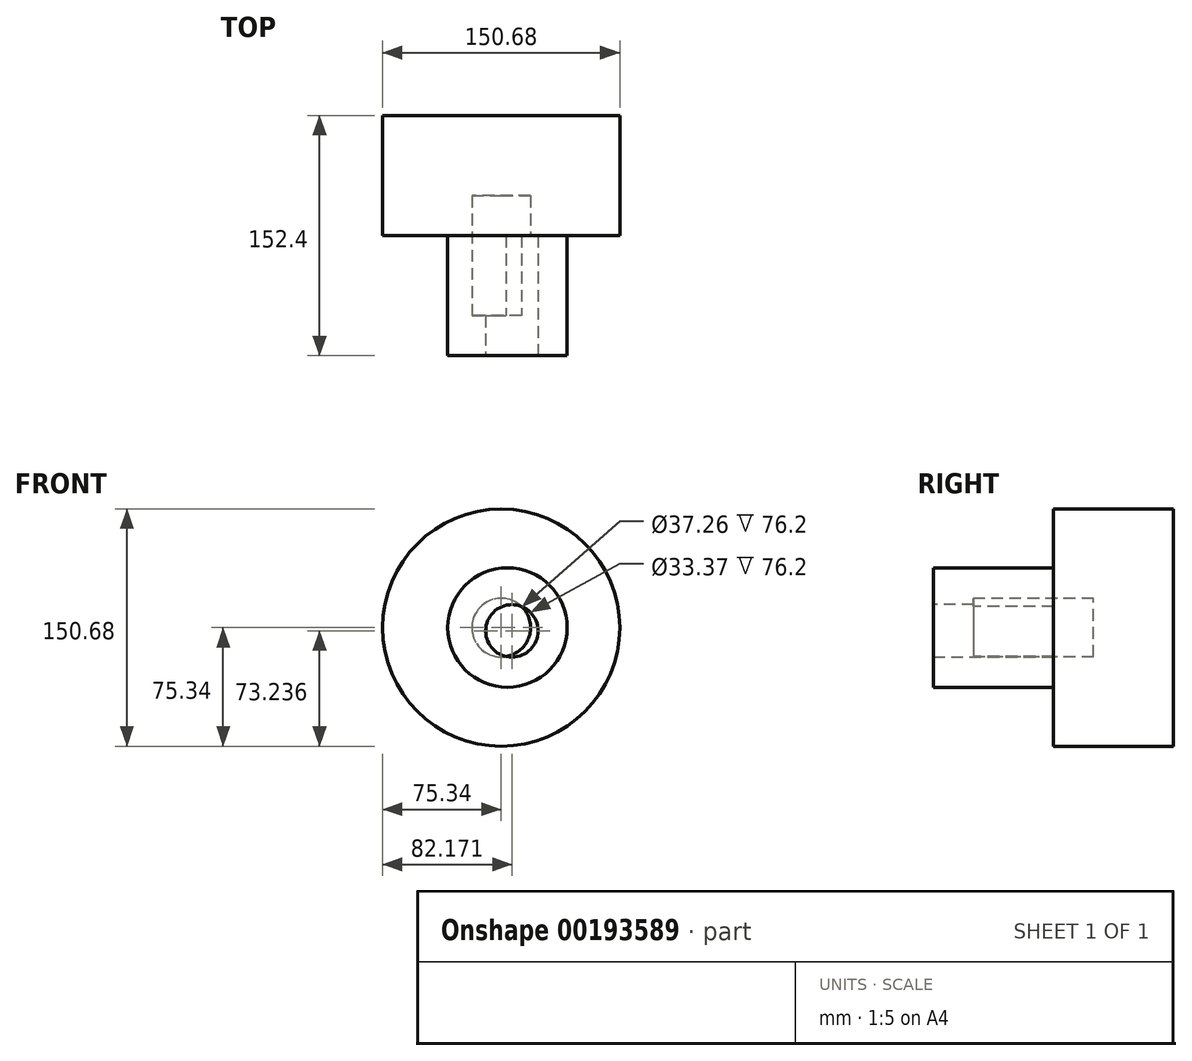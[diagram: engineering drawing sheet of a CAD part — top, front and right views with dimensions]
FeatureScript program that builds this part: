
annotation { "Feature Type Name" : "Feature", "Feature Type Description" : "" }
export const myFeature = defineFeature(function(context is Context, id is Id, definition is map)
    precondition{}
    {
        {
            var Q0;
            Q0=qCreatedBy(makeId("Front.planeOp"),FACE);
            var sketch = newSketch(context, id + "F0", { "sketchPlane" : qUnion([Q0])});
            skPoint(sketch, "E0.middle", {"position": v(0, 0) * mm});
            skCircle(sketch, "E1", {"center": v(0, 0) * mm, "radius": 75.34 * mm});
            skSolve(sketch);
        }
        {
            var Q0;
            Q0=makeQuery(id+"F0.imprint","IMPRINT",FACE,{"disambiguationData":[TD([[makeQuery(id+"F0.imprint","IMPRINT",EDGE,{"derivedFrom":sQuery(id+"F0.wireOp",EDGE,"E1")}),1.0]])]});
            extrude(context, id + "F1", {"entities" : qUnion([Q0]), "depth" : 76.2 * mm});
        }
        {
            var Q0;
            Q0=qCreatedBy(makeId("Front.planeOp"),FACE);
            var sketch = newSketch(context, id + "F2", { "sketchPlane" : qUnion([Q0])});
            skCircle(sketch, "E2", {"center": v(3.93, 0) * mm, "radius": 37.95 * mm});
            skSolve(sketch);
        }
        {
            var Q0;
            Q0 = qSketchRegion(id + "F2", true);
            extrude(context, id + "F3", {"entities" : qUnion([Q0]), "operationType" : NewBodyOperationType.ADD, "depth" : 127 * mm});
        }
        {
            var Q0;
            Q0=makeQuery(id+"F3.opExtrude","CAP_FACE",FACE,{"disambiguationData":[OSD([sQuery(id+"F2.wireOp",EDGE,"E2")])],"isStart":false});
            var sketch = newSketch(context, id + "F4", { "sketchPlane" : qUnion([Q0])});
            skSolve(sketch);
        }
        {
            var Q0;
            Q0=makeQuery(id+"F4.imprint","IMPRINT",FACE,{"disambiguationData":[TD([[makeQuery(id+"F4.imprint","IMPRINT",EDGE,{"derivedFrom":makeQuery(id+"F3.opExtrude","CAP_EDGE",EDGE,{"disambiguationData":[OSD([sQuery(id+"F2.wireOp",EDGE,"E2")])],"isStart":false})}),1.0]])]});
            var sketch = newSketch(context, id + "F5", { "sketchPlane" : qUnion([Q0])});
            skCircle(sketch, "E3", {"center": v(0, 0) * mm, "radius": 18.63 * mm});
            skSolve(sketch);
        }
        {
            var Q0;
            Q0=makeQuery(id+"F5.imprint","IMPRINT",FACE,{"disambiguationData":[TD([[makeQuery(id+"F5.imprint","IMPRINT",EDGE,{"derivedFrom":sQuery(id+"F5.wireOp",EDGE,"E3")}),1.0]])]});
            extrude(context, id + "F6", {"entities" : qUnion([Q0]), "operationType" : NewBodyOperationType.REMOVE, "oppositeDirection" : true, "depth" : 76.2 * mm});
        }
        {
            var Q0;
            Q0=makeQuery(id+"F4.imprint","IMPRINT",FACE,{"disambiguationData":[TD([[makeQuery(id+"F4.imprint","IMPRINT",EDGE,{"derivedFrom":makeQuery(id+"F3.opExtrude","CAP_EDGE",EDGE,{"disambiguationData":[OSD([sQuery(id+"F2.wireOp",EDGE,"E2")])],"isStart":false})}),1.0]])]});
            extrude(context, id + "F7", {"entities" : qUnion([Q0]), "operationType" : NewBodyOperationType.ADD, "depth" : 76.2 * mm});
        }
        {
            var Q0;
            Q0=makeQuery(id+"F7.opExtrude","CAP_FACE",FACE,{"disambiguationData":[OSD([sQuery(id+"F2.wireOp",EDGE,"E2")])],"isStart":false});
            extrude(context, id + "F8", {"entities" : qUnion([Q0]), "operationType" : NewBodyOperationType.REMOVE, "oppositeDirection" : true, "depth" : 50.8 * mm});
        }
        {
            var Q0;
            Q0=makeQuery(id+"F8.boolean.opBoolean","COPY",FACE,{"derivedFrom":makeQuery(id+"F8.opExtrude","CAP_FACE",FACE,{"disambiguationData":[OSD([sQuery(id+"F2.wireOp",EDGE,"E2")])],"isStart":false})});
            var sketch = newSketch(context, id + "F9", { "sketchPlane" : qUnion([Q0])});
            skCircle(sketch, "E4", {"center": v(6.83, -2.1) * mm, "radius": 16.69 * mm});
            skSolve(sketch);
        }
        {
            var Q0;
            Q0=makeQuery(id+"F9.imprint","IMPRINT",FACE,{"disambiguationData":[TD([[makeQuery(id+"F9.imprint","IMPRINT",EDGE,{"derivedFrom":sQuery(id+"F9.wireOp",EDGE,"E4")}),1.0]])]});
            extrude(context, id + "F10", {"entities" : qUnion([Q0]), "operationType" : NewBodyOperationType.REMOVE, "oppositeDirection" : true, "depth" : 76.2 * mm});
        }
    });
